# Revit family: 1121xxx Mashiko Round 300 LED (UL)
name_source: partatom
category: Lighting Fixtures
revit_build: Autodesk Revit 2018 (Build: 20170223_1515(x64)
units: mm (PartAtom-declared; Revit-internal decimal feet)

## family parameters
Always vertical = Yes
Cut with Voids When Loaded = No
Host = Ceiling
Light Source = Yes
OmniClass Number = 23.80.70.11
OmniClass Title = Luminaries for Internal Lighting
Part Type = Normal
Room Calculation Point = No
Round Connector Dimension = Use Diameter
Shared = No

## types (2) — shared parameters
ADA compliant = Yes
Apparent Load = 18 VA
Color Filter = 16777215
Dimmable = Yes
Dimming Lamp Color Temperature Shift = <None>
Dimming Method = 1-10V
Driver Included = Yes (Integral)
Driver Required = No
Efficacy (lm/w) = 53
Electrical Class = 1
Lamp = LED
Light Source Fixed = Yes
Location / IP Rating = Wet
Main Material = Metal - Mild Steel
Manufacturer URL - Europe and Rest of World = www.astrolighting.com
Manufacturer URL - North America = us.astrolighting.com
Power (Watts) = 17.9
Product CCT = 3000k
Product CRI = 90
Product Dimensions (MM) = 86x300x300
Product Location = Bathroom
Product Name = Mashiko Round 300 LED
Product SKU = 1121048
Product URL = https://us.astrolighting.com
Product Weight (KG) = 2 mm  [stored 0.00656168 ft]
Tilt Angle = 0.00°

## per-type parameters (varying)
| type | Main Finish | Photometric Web File |
| Astro Mashiko Round 300 LED Bronze | Bronze | generic |
| Astro Mashiko Round 300 LED Polished Chrome | Polished Chrome |  |

note: [stored X ft] marks values corroborated as IEEE doubles in the binary element streams (Revit-internal decimal feet)

## geometry (parser evidence)
native form markers: Sweep x2
no freeform markers — native parametric forms only
